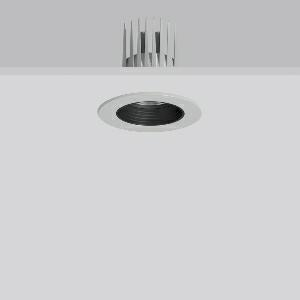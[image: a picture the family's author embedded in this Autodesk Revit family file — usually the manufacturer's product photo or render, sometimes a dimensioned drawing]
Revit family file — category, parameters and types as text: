
# Revit family: heledon_mini_e_901746_004_1_76_afd9
name_source: partatom
category: Lighting Fixtures
units: mm (PartAtom-declared; Revit-internal decimal feet)

## family parameters
Cut with Voids When Loaded = No
Host = Face
Light Source = No
Part Type = Normal
Room Calculation Point = No
Round Connector Dimension = Use Diameter
Shared = No

## types (1)
- HELEDON mini E (1 x LED Modul 940, 2450 lm, 4000)
    Apparent Load = 20 VA
    Approval mark = CE
    CIE Flux Codes = 80 99 100 100 100
    Color Rendering = 92
    Color Temperature = 4000
    Default Elevation = 1800 mm
    Description = Series: HELEDON mini
Round recessed downlight. Housing: die-cast aluminium, powder-coated. Black plastic ring and recessed LED to prevent glare from the side. Optical assembly with lens made of plastic (polycarbonate) for the best homogeneous light distribution - can be changed without tools. Best colour rendering index Ra>90. Suitable for Recessed ceiling mounting. Installation without tools thanks to spring fastening system. Including separate LED converter with connecting cable 600 mm.High quality converter without flickering and stroboscopic effect. Through-wiring box (5 pole) available as accessory. The following accessories can be mounted without use of tools: interchangeable lenses, decorative glasses, honeycomb louvre, clear and frosted diffusers, white interchangeable plastic ring. 
Colour: silver
Diameter: 124 mm
Height: 3 mm
Cut-out diameter: 114 mm
Recess height: 170 mm
Luminaire: recess height: 120 mm
Lamp: LED
Socket: without socket
Colour temperature: 4000K
Colour rendering index (CRI): 92
System power: 20 W
Rated luminous flux: 2450 lm
Luminous efficiency: 123 lm/W
Control gear: Converter, dimmable, DALI
Protection class: II
Type of protection: IP 20
    Height = 0 mm  [stored 0 ft]
    Lamp = 1 x LED Modul 940
    Lamp Light Flux = 2450 lm
    Lamp count = 1
    Length = 124 mm  [stored 0.406824 ft]
    Lifetime = 50000 h
    Luminous efficacy = 123 lm/W
    Manufacturer = RZB
    ModVariant = No
    Model = 901746.004.1.76
    Mounting Place = Ceiling
    Mounting Type = Recessed
    Number of Poles = 1
    OnlyDefault = Yes
    Power Factor = 1
    Product Name = HELEDON mini E
    Product group = Recessed downlights
    ProductGroupID = 402
    Protection Class = Protection class II
    Protection Degree = IP 20
    RLX_Detail_Level = 1
    RLX_Emergency_Light_Flux = 0 lm
    RLX_Emergency_Type = 0
    RLX_Emergency_Type_DB = No
    RlxData = <blob elided: 124953 chars, md5=a3195ab0>
    Socket = socket
    Standby Power = 0 W
    System Light Flux = 2450 lm
    System Power = 20 W
    Type Comments = Product without accessories
    Type Image = 901656.004.jpg
    URL = http://relux.com
    VarID = ---
    Voltage = 230 V
    Voltage Range = 220-240 V
    Weight = 0.00 kg
    Width = 0 mm  [stored 0 ft]

note: [stored X ft] marks values corroborated as IEEE doubles in the binary element streams (Revit-internal decimal feet)

## geometry (parser evidence)
native form markers: Blend x4, Sweep x12
no freeform markers — native parametric forms only
